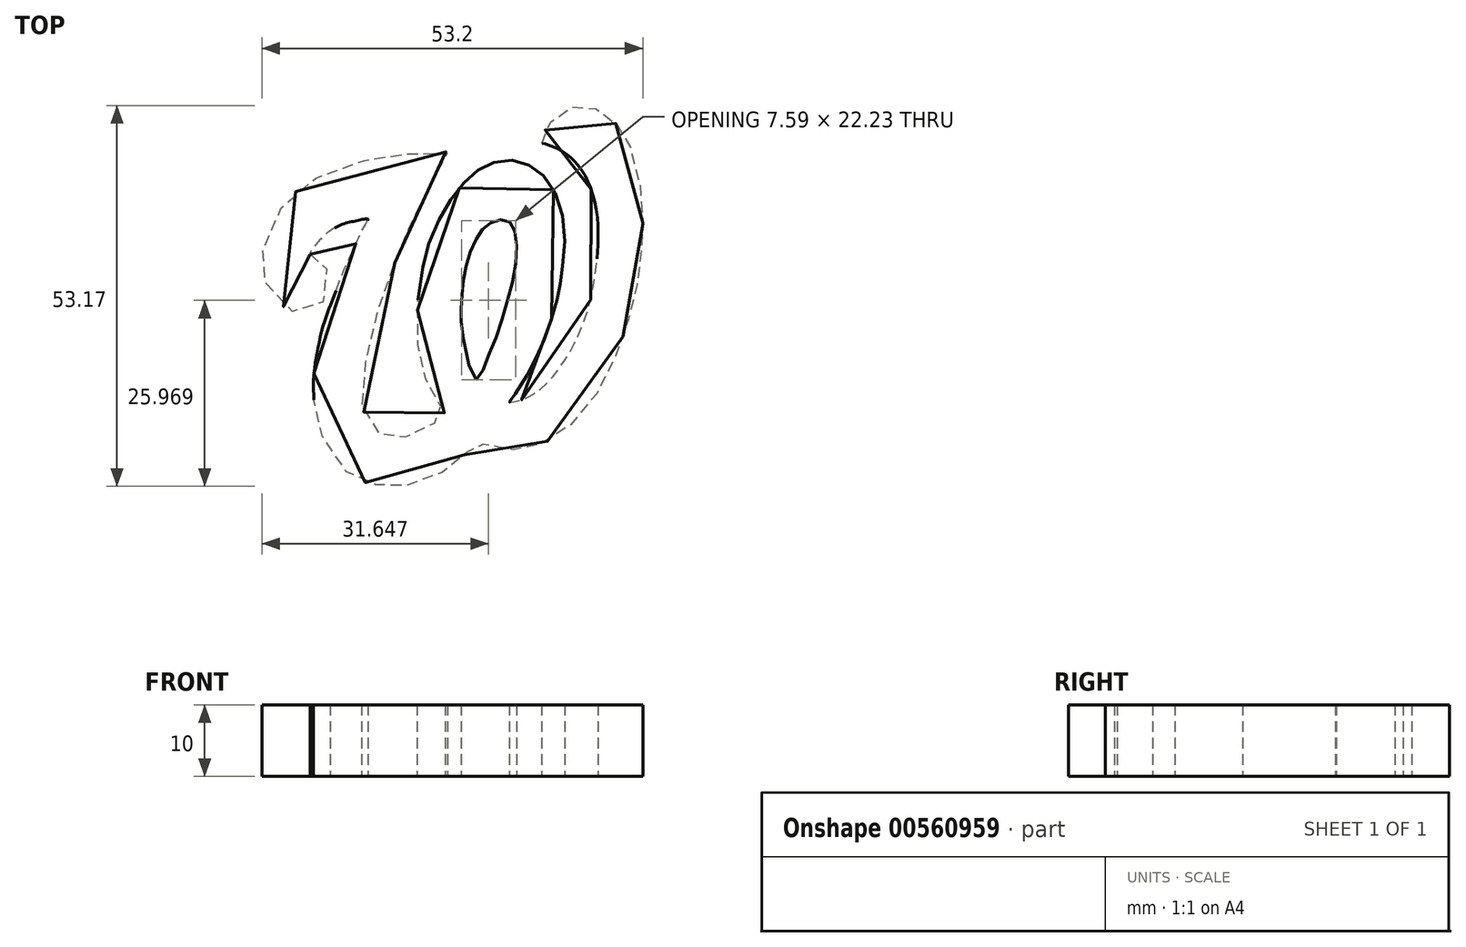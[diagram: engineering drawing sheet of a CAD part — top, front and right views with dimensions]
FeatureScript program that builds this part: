
annotation { "Feature Type Name" : "Feature", "Feature Type Description" : "" }
export const myFeature = defineFeature(function(context is Context, id is Id, definition is map)
    precondition{}
    {
        {
            var Q0;
            Q0=qCreatedBy(makeId("Top.planeOp"),FACE);
            var sketch = newSketch(context, id + "F0", { "sketchPlane" : qUnion([Q0])});
            skFitSpline(sketch, "E0", {"points": [v(8.98, 33.79) * mm, v(9.74, 33.36) * mm, v(10.47, 32.73) * mm, v(11.28, 31.69) * mm, v(11.76, 29.64) * mm, v(10.5, 26.78) * mm, v(8.62, 25.84) * mm, v(5.97, 26.02) * mm, v(3.16, 28.88) * mm, v(2.45, 30.8) * mm, v(2.25, 33.2) * mm, v(2.98, 36.52) * mm, v(5.33, 40.82) * mm, v(8.42, 43.63) * mm, v(13.68, 46.16) * mm, v(18.47, 47.28) * mm, v(22.26, 47.8) * mm, v(27.98, 48.09) * mm, v(28.13, 48.06) * mm, v(27.42, 46.85) * mm, v(25.65, 43.38) * mm, v(23.96, 39.99) * mm, v(21.73, 35.13) * mm, v(21.15, 33.56) * mm, v(19.6, 29.67) * mm, v(17.7, 23.44) * mm, v(16.57, 18.05) * mm, v(16.16, 13.37) * mm, v(16.42, 11.88) * mm, v(17.66, 9.55) * mm, v(19.45, 8.39) * mm, v(21.12, 8.18) * mm, v(22.54, 8.34) * mm, v(24.2, 8.82) * mm, v(26.59, 10.46) * mm, v(27.73, 11.68) * mm, v(27.8, 12) * mm, v(27.35, 12.36) * mm, v(26, 14.46) * mm, v(25.2, 16.13) * mm, v(24.64, 17.95) * mm, v(24.06, 20.94) * mm, v(23.93, 25.54) * mm, v(24.16, 28.43) * mm, v(24.39, 30.07) * mm, v(24.94, 33.13) * mm, v(26.59, 37.81) * mm, v(28.74, 41.56) * mm, v(30.91, 44.26) * mm, v(32.91, 45.83) * mm, v(35.27, 46.77) * mm, v(37.82, 46.9) * mm, v(40, 45.99) * mm, v(42, 44.26) * mm, v(43.8, 40.85) * mm, v(44.55, 36.17) * mm, v(44.1, 31.41) * mm, v(43.83, 29.35) * mm, v(43.38, 27.27) * mm, v(42.52, 24.3) * mm, v(41.27, 20.92) * mm, v(40.14, 18.61) * mm, v(38.2, 15.1) * mm, v(37.01, 13.4) * mm, v(36.87, 13.2) * mm, v(36.8, 13.12) * mm, v(37.23, 13.16) * mm, v(38.62, 13.5) * mm, v(40.5, 14.52) * mm, v(43.24, 17.18) * mm, v(45.82, 21.2) * mm, v(46.94, 23.75) * mm, v(47.77, 26.07) * mm, v(48.48, 29.12) * mm, v(49.05, 33.07) * mm, v(49.14, 35.18) * mm, v(49.2, 37.17) * mm, v(48.93, 40.12) * mm, v(48.4, 42.18) * mm, v(48.2, 42.9) * mm, v(47.44, 44.63) * mm, v(46.37, 46.22) * mm, v(45.46, 47.22) * mm, v(44.44, 48.05) * mm, v(43.04, 48.76) * mm, v(41.49, 49.3) * mm, v(41.29, 49.33) * mm, v(41.49, 50.43) * mm, v(42.1, 51.66) * mm, v(43.15, 52.95) * mm, v(44.31, 53.82) * mm, v(45.78, 54.4) * mm, v(47.18, 54.56) * mm, v(48.45, 54.29) * mm, v(49.48, 53.84) * mm, v(50.6, 53.13) * mm, v(52.08, 51.6) * mm, v(52.56, 50.9) * mm, v(53.3, 49.58) * mm, v(54.23, 47.12) * mm, v(55.07, 43.34) * mm, v(55.3, 41.05) * mm, v(55.4, 38.83) * mm, v(55.43, 37.17) * mm, v(55.26, 34.51) * mm, v(54.95, 31.49) * mm, v(54.5, 28.9) * mm, v(53.84, 26.1) * mm, v(53.07, 23.62) * mm, v(51.95, 20.4) * mm, v(50.48, 16.94) * mm, v(48.41, 13.47) * mm, v(46.2, 10.79) * mm, v(43.24, 8.32) * mm, v(41.63, 7.47) * mm, v(39.48, 6.72) * mm, v(38, 6.51) * mm, v(35.84, 6.51) * mm, v(33.95, 6.92) * mm, v(32.1, 7.7) * mm, v(31.82, 7.72) * mm, v(31.16, 6.62) * mm, v(29.75, 5.1) * mm, v(28.28, 3.9) * mm, v(25.41, 2.3) * mm, v(22.37, 1.5) * mm, v(20.58, 1.4) * mm, v(18.33, 1.6) * mm, v(16.56, 1.95) * mm, v(14.21, 3.3) * mm, v(11.6, 6.4) * mm, v(10.2, 9.75) * mm, v(9.58, 12.63) * mm, v(9.45, 16.34) * mm, v(9.8, 19.34) * mm, v(10.87, 24.09) * mm, v(11.96, 27.1) * mm, v(13.51, 31.17) * mm, v(14.93, 34.32) * mm, v(16.1, 36.93) * mm, v(16.97, 38.5) * mm, v(16.99, 38.76) * mm, v(15.72, 38.54) * mm, v(13.01, 37.8) * mm, v(10.46, 35.97) * mm, v(9.38, 34.66) * mm, v(8.98, 33.79) * mm]});
            skFitSpline(sketch, "E1", {"points": [v(32.13, 16.24) * mm, v(33.4, 18.37) * mm, v(34.97, 22.32) * mm, v(36.54, 27.38) * mm, v(37.65, 32.08) * mm, v(37.7, 36.23) * mm, v(37.1, 38) * mm, v(36.13, 38.61) * mm, v(34.66, 38.4) * mm, v(33.35, 37.65) * mm, v(32.39, 36.28) * mm, v(31.22, 33.8) * mm, v(30.51, 30.97) * mm, v(30.16, 28.03) * mm, v(30.06, 25.45) * mm, v(30.31, 22.37) * mm, v(32.13, 16.24) * mm]});
            skSolve(sketch);
        }
        {
            var Q0;
            Q0=makeQuery(id+"F0.imprint","IMPRINT",FACE,{"disambiguationData":[TD([[makeQuery(id+"F0.imprint","IMPRINT",EDGE,{"derivedFrom":sQuery(id+"F0.wireOp",EDGE,"E0")}),-1.0]])]});
            extrude(context, id + "F1", {"entities" : qUnion([Q0]), "depth" : 10 * mm, "offsetDistance" : 25 * mm});
        }
    });
